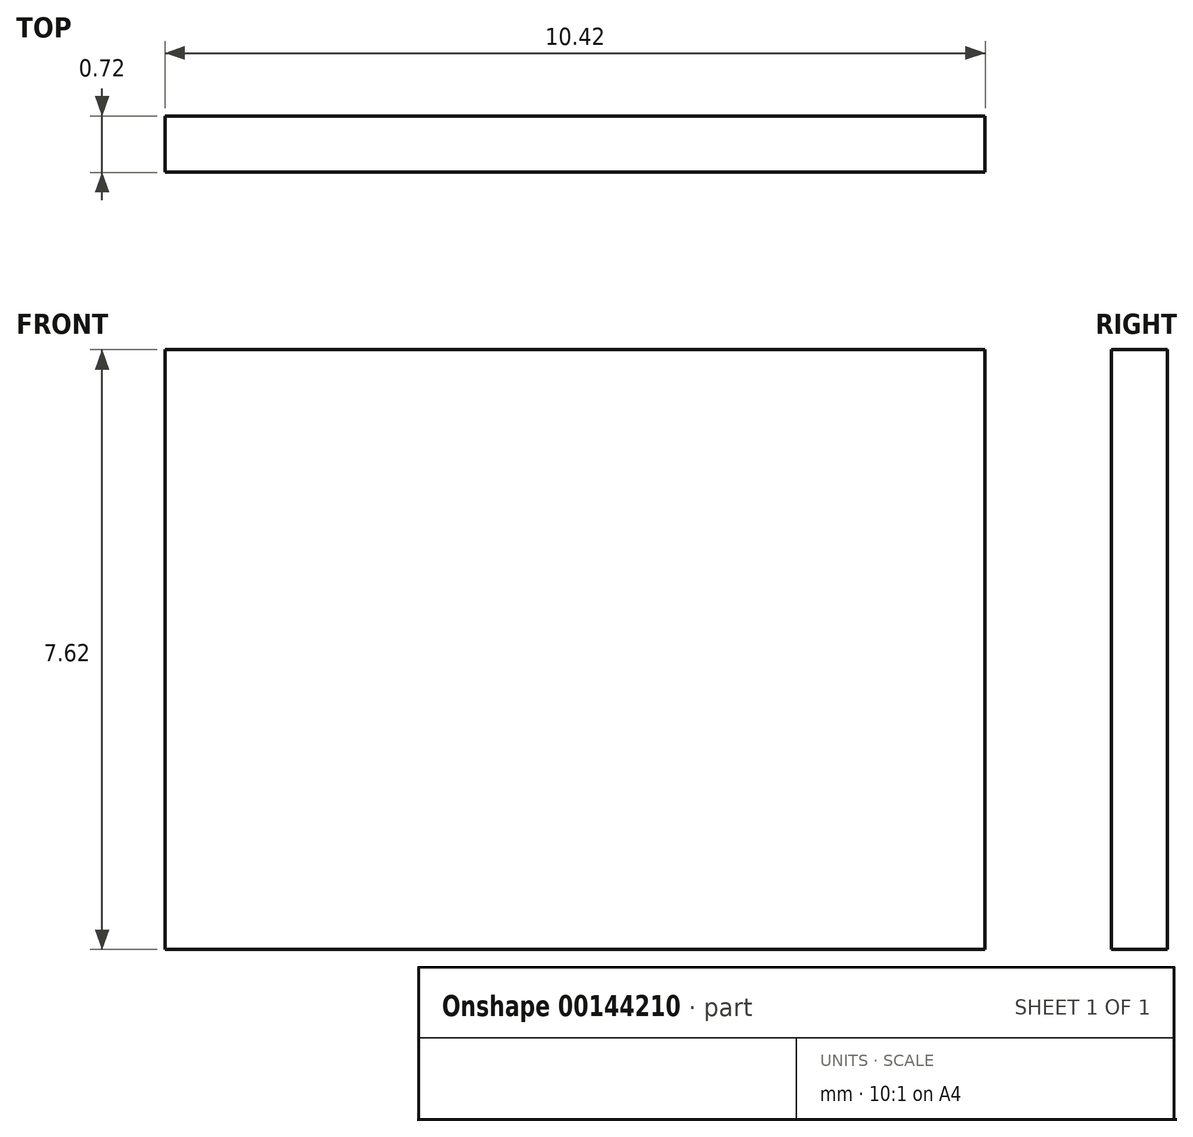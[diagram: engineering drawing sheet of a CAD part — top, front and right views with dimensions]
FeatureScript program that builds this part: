
annotation { "Feature Type Name" : "Feature", "Feature Type Description" : "" }
export const myFeature = defineFeature(function(context is Context, id is Id, definition is map)
    precondition{}
    {
        {
            var Q0;
            Q0=qCreatedBy(makeId("Front.planeOp"),FACE);
            var sketch = newSketch(context, id + "F0", { "sketchPlane" : qUnion([Q0])});
            skLineSegment(sketch, "E0.bottom", {"start": v(5.2, 3.81) * mm, "end": v(-5.2, 3.81) * mm});
            skLineSegment(sketch, "E0.top", {"start": v(5.2, -3.81) * mm, "end": v(-5.2, -3.81) * mm});
            skLineSegment(sketch, "E0.left", {"start": v(5.2, 3.81) * mm, "end": v(5.2, -3.81) * mm});
            skLineSegment(sketch, "E0.right", {"start": v(-5.2, 3.81) * mm, "end": v(-5.2, -3.81) * mm});
            skPoint(sketch, "E0.middle", {"position": v(0, 0) * mm});
            skSolve(sketch);
        }
        {
            var Q0;
            Q0=qSketchRegion(id+"F0",true);
            extrude(context, id + "F1", {"entities" : qUnion([Q0]), "endBound" : BoundingType.SYMMETRIC, "depth" : 0.71 * mm});
        }
    });
